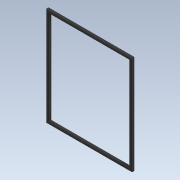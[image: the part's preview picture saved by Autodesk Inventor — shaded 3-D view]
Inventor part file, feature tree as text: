
AUTODESK INVENTOR PART (.ipt)
format: ipt  version: 2020 (Build 240168000, 168)  size: 97,280 bytes
history: native  units: mm
features: extrude x1, fillet x1, sketch x1
ambient origin geometry x8: Origin, YZ Plane, XZ Plane, XY Plane, X Axis, Y Axis, Z Axis, Center Point
bodies: Volumenkörper1 (feature_tree)
feature tree (3):
  extrude  "Extrusion1"  Depth=92.0mm
  fillet  "Rundung1"  Radius=98.0mm
  sketch  "Skizze1"  dims[d0=107.0mm d1=92.0mm d2=98.0mm d3=113.0mm d4=3.0mm d5=3.0mm d6=3.0mm d7=0.0mm d8=1.0mm]
